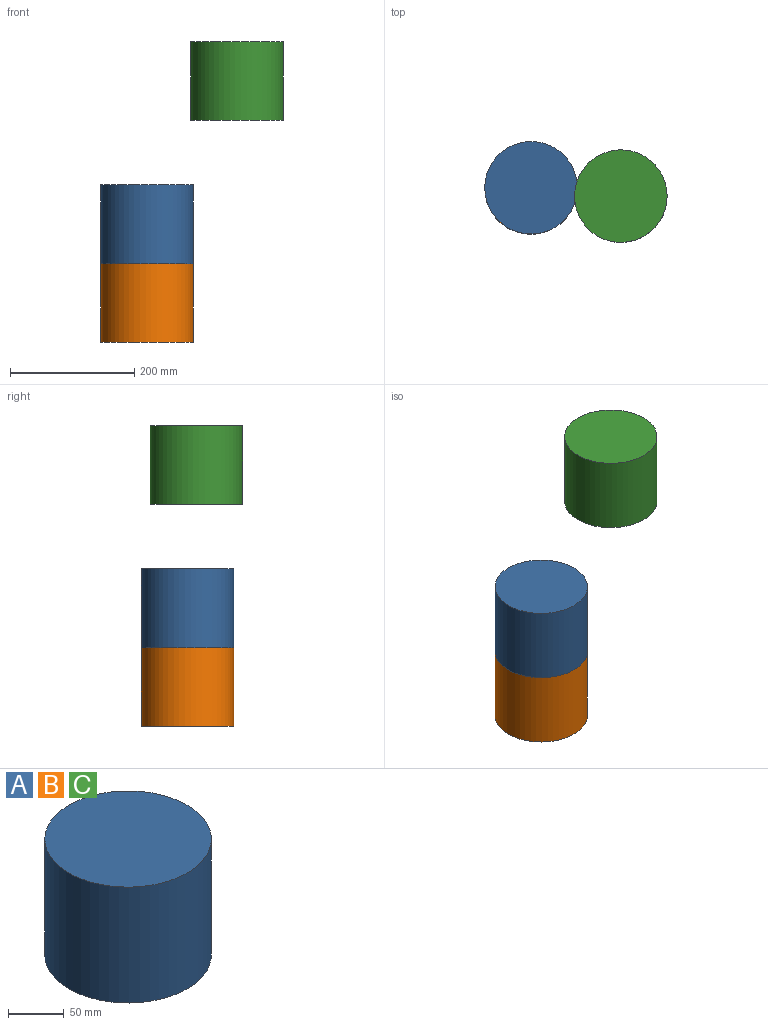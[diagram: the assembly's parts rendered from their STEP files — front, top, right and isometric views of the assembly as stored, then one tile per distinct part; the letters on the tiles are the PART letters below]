
ASSEMBLY  parts=3 mates=1
PART A: 3 faces, bbox 149.1x149.1x127 mm
  f0: cylinder r=74.57mm len=149.14mm, axis (0,0,-1), area 59504.5mm2, adj f1,f2
  f1: plane 149.14x149.14mm, normal (0,0,-1), area 17469.6mm2, adj f0
  f2: plane 149.14x149.14mm, normal (0,0,1), area 17469.6mm2, adj f0
PART B: same geometry as A
PART C: same geometry as A
PLACE A t=(0,0,127)mm
PLACE B at identity
PLACE C t=(144.81,-13.87,357.91)mm
MATE fastened A.f0 <-> B.f0  axis (0,0,-1) through (0,0,127)mm
